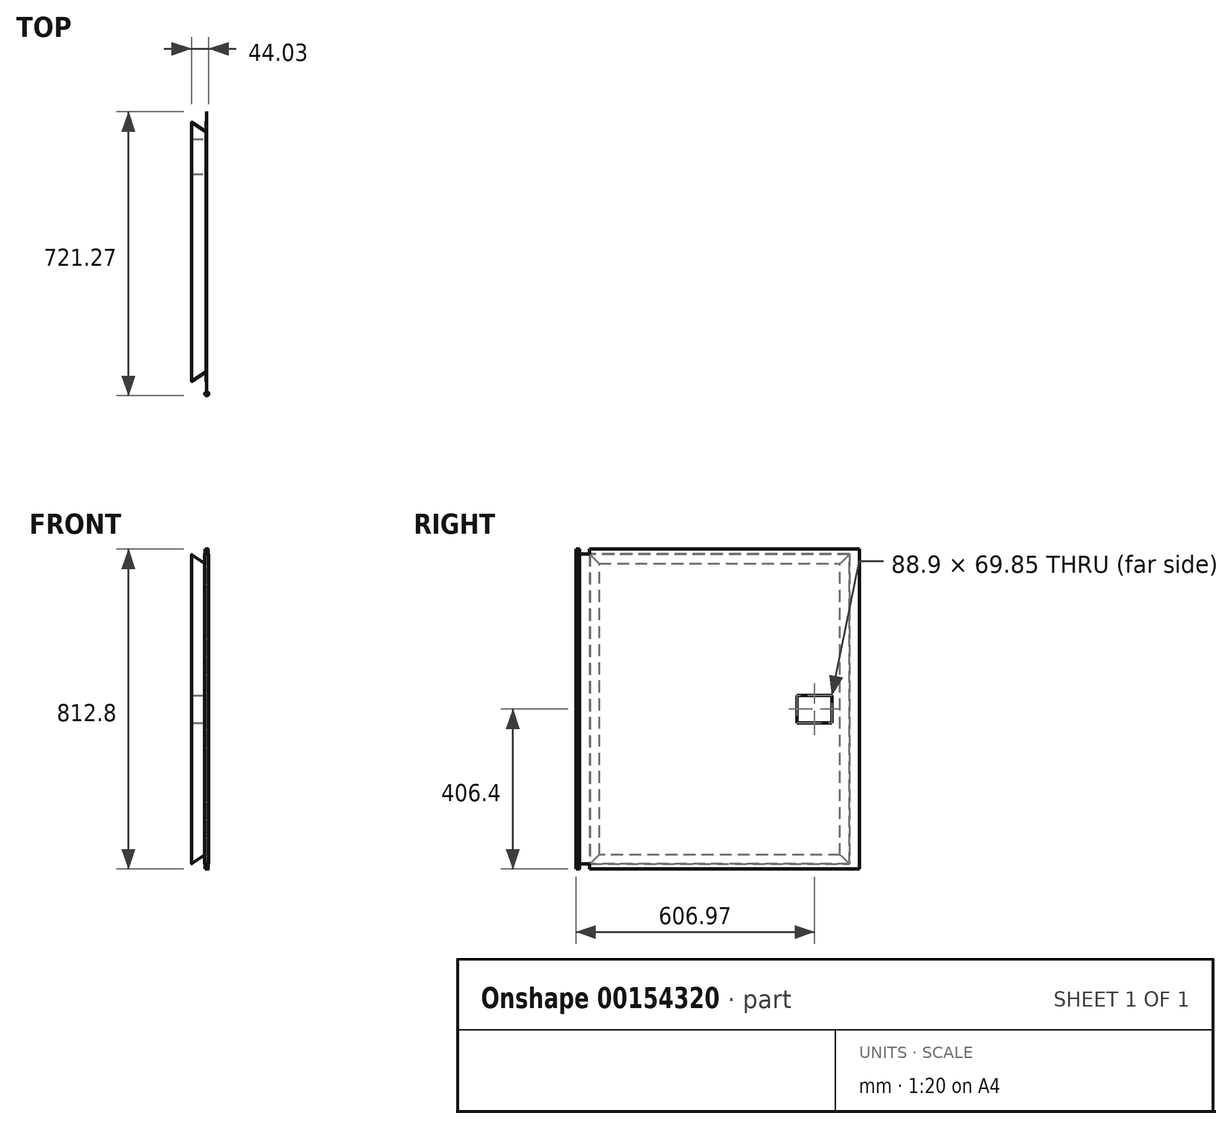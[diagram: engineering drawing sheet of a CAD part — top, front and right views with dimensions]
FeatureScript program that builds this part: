
annotation { "Feature Type Name" : "Feature", "Feature Type Description" : "" }
export const myFeature = defineFeature(function(context is Context, id is Id, definition is map)
    precondition{}
    {
        {
            var Q0;
            Q0=qCreatedBy(makeId("Right.planeOp"),FACE);
            var sketch = newSketch(context, id + "F0", { "sketchPlane" : qUnion([Q0])});
            skLineSegment(sketch, "E0.bottom", {"start": v(-330.2, 406.4) * mm, "end": v(355.6, 406.4) * mm});
            skLineSegment(sketch, "E0.left", {"start": v(-355.6, 393.7) * mm, "end": v(-355.6, -393.7) * mm});
            skLineSegment(sketch, "E0.right", {"start": v(355.6, 406.4) * mm, "end": v(355.6, -406.4) * mm});
            skPoint(sketch, "E0.middle", {"position": v(0, 0) * mm});
            skLineSegment(sketch, "E1", {"start": v(-355.6, 393.7) * mm, "end": v(-330.2, 393.7) * mm});
            skLineSegment(sketch, "E2", {"start": v(-330.2, 393.7) * mm, "end": v(-330.2, 406.4) * mm});
            skLineSegment(sketch, "E3", {"start": v(355.6, -406.4) * mm, "end": v(-330.2, -406.4) * mm});
            skLineSegment(sketch, "E4", {"start": v(-330.2, -406.4) * mm, "end": v(-330.2, -393.7) * mm});
            skLineSegment(sketch, "E5", {"start": v(-330.2, -393.7) * mm, "end": v(-355.6, -393.7) * mm});
            skLineSegment(sketch, "E6", {"start": v(-355.6, 0) * mm, "end": v(355.6, 0) * mm});
            skSolve(sketch);
        }
        {
            var Q0;
            Q0 = qSketchRegion(id + "F0", true);
            extrude(context, id + "F1", {"entities" : qUnion([Q0]), "oppositeDirection" : true, "depth" : 0.89 * mm});
        }
        {
            var Q0;
            Q0=makeQuery(id+"F1.opExtrude","CAP_FACE",FACE,{"disambiguationData":[OSD([sQuery(id+"F0.wireOp",EDGE,"E0.bottom"),sQuery(id+"F0.wireOp",EDGE,"E0.top"),sQuery(id+"F0.wireOp",EDGE,"E0.left"),sQuery(id+"F0.wireOp",EDGE,"E0.right")])],"isStart":false});
            var sketch = newSketch(context, id + "F2", { "sketchPlane" : qUnion([Q0])});
            skLineSegment(sketch, "E7.bottom", {"start": v(-330.2, 393.7) * mm, "end": v(330.2, 393.7) * mm});
            skLineSegment(sketch, "E7.top", {"start": v(-330.2, -393.7) * mm, "end": v(330.2, -393.7) * mm});
            skLineSegment(sketch, "E7.left", {"start": v(-330.2, 393.7) * mm, "end": v(-330.2, -393.7) * mm});
            skLineSegment(sketch, "E7.right", {"start": v(330.2, 393.7) * mm, "end": v(330.2, -393.7) * mm});
            skPoint(sketch, "E7.middle", {"position": v(0, 0) * mm});
            skSolve(sketch);
        }
        {
            var Q0;
            Q0 = qSketchRegion(id + "F2", true);
            extrude(context, id + "F3", {"entities" : qUnion([Q0]), "operationType" : NewBodyOperationType.ADD, "depth" : 38.1 * mm});
        }
        {
            var Q0;
            Q0=makeQuery(id+"F3.opExtrude","SWEPT_FACE",FACE,{"disambiguationData":[OSD([sQuery(id+"F2.wireOp",EDGE,"E7.left")])]});
            var sketch = newSketch(context, id + "F4", { "sketchPlane" : qUnion([Q0])});
            skLineSegment(sketch, "E8", {"start": v(38.99, 393.7) * mm, "end": v(38.99, -393.7) * mm});
            skLineSegment(sketch, "E9", {"start": v(38.99, 393.7) * mm, "end": v(2.13, 368.85) * mm});
            skLineSegment(sketch, "E10", {"start": v(2.13, 393.7) * mm, "end": v(2.13, -393.7) * mm});
            skLineSegment(sketch, "E11", {"start": v(38.99, -393.7) * mm, "end": v(2.13, -368.85) * mm});
            skSolve(sketch);
        }
        {
            var Q0;
            {var subQ3=sQuery(id+"F4.wireOp",EDGE,"E11");Q0=makeQuery(id+"F4.imprint","IMPRINT",FACE,{"disambiguationData":[TD([[makeQuery(id+"F4.imprint","IMPRINT",EDGE,{"derivedFrom":subQ3}),1.0]])]});}
            var Q1;
            {var subQ0=sQuery(id+"F4.wireOp",EDGE,"E9");Q1=makeQuery(id+"F4.imprint","IMPRINT",FACE,{"disambiguationData":[TD([[makeQuery(id+"F4.imprint","IMPRINT",EDGE,{"derivedFrom":subQ0}),-1.0]])]});}
            extrude(context, id + "F5", {"entities" : qUnion([Q0, Q1]), "operationType" : NewBodyOperationType.REMOVE, "endBound" : BoundingType.THROUGH_ALL, "oppositeDirection" : true, "depth" : 25.4 * mm});
        }
        {
            var Q0;
            {var subQ0=sQuery(id+"F4.wireOp",EDGE,"E10");var subQ2=sQuery(id+"F2.wireOp",EDGE,"E7.bottom");Q0=makeQuery(id+"F5.boolean.opBoolean","SPLIT",FACE,{"disambiguationData":[TD([makeQuery(id+"F5.opExtrude","SWEPT_FACE",FACE,{"disambiguationData":[OSD([subQ0]),TDD([makeQuery(id+"F4.imprint","IMPRINT",EDGE,{"disambiguationData":[TD([[makeQuery(id+"F4.imprint","INTERSECT",VERTEX,{"derivedFrom":[sQuery(id+"F4.wireOp",EDGE,"E9"),subQ0]}),1.0]])],"derivedFrom":subQ0})])]})])],"derivedFrom":makeQuery(id+"F3.opExtrude","SWEPT_FACE",FACE,{"disambiguationData":[OSD([subQ2])]})});}
            var sketch = newSketch(context, id + "F6", { "sketchPlane" : qUnion([Q0])});
            skLineSegment(sketch, "E12", {"start": v(-38.99, 330.2) * mm, "end": v(-2.13, 305.35) * mm});
            skLineSegment(sketch, "E13", {"start": v(-38.99, 330.2) * mm, "end": v(-2.13, 330.2) * mm});
            skLineSegment(sketch, "E14", {"start": v(-2.13, 305.35) * mm, "end": v(-2.13, 330.2) * mm});
            skLineSegment(sketch, "E15", {"start": v(-2.13, -305.35) * mm, "end": v(-2.13, -330.2) * mm});
            skLineSegment(sketch, "E16", {"start": v(-2.13, -330.2) * mm, "end": v(-38.99, -330.2) * mm});
            skLineSegment(sketch, "E17", {"start": v(-38.99, -330.2) * mm, "end": v(-2.13, -305.35) * mm});
            skSolve(sketch);
        }
        {
            var Q0;
            Q0=makeQuery(id+"F6.imprint","IMPRINT",FACE,{"disambiguationData":[TD([[makeQuery(id+"F6.imprint","IMPRINT",EDGE,{"derivedFrom":sQuery(id+"F6.wireOp",EDGE,"E15")}),1.0]])]});
            var Q1;
            Q1=makeQuery(id+"F6.imprint","IMPRINT",FACE,{"disambiguationData":[TD([[makeQuery(id+"F6.imprint","IMPRINT",EDGE,{"derivedFrom":sQuery(id+"F6.wireOp",EDGE,"E12")}),1.0]])]});
            extrude(context, id + "F7", {"entities" : qUnion([Q0, Q1]), "operationType" : NewBodyOperationType.REMOVE, "endBound" : BoundingType.THROUGH_ALL, "oppositeDirection" : true, "depth" : 25.4 * mm});
        }
        {
            var Q0;
            Q0=makeQuery(id+"F3.opExtrude","CAP_EDGE",EDGE,{"disambiguationData":[OSD([sQuery(id+"F2.wireOp",EDGE,"E7.top")])],"isStart":false});
            var Q1;
            Q1=makeQuery(id+"F3.opExtrude","CAP_EDGE",EDGE,{"disambiguationData":[OSD([sQuery(id+"F2.wireOp",EDGE,"E7.left")])],"isStart":false});
            var Q2;
            Q2=makeQuery(id+"F3.opExtrude","CAP_EDGE",EDGE,{"disambiguationData":[OSD([sQuery(id+"F2.wireOp",EDGE,"E7.bottom")])],"isStart":false});
            var Q3;
            Q3=makeQuery(id+"F3.opExtrude","CAP_EDGE",EDGE,{"disambiguationData":[OSD([sQuery(id+"F2.wireOp",EDGE,"E7.right")])],"isStart":false});
            fillet(context, id + "F8", {"entities" : qUnion([Q0, Q1, Q2, Q3]), "radius" : 1.27 * mm, "tangentPropagation" : true, "allowEdgeOverflow" : false});
        }
        {
            var Q0;
            Q0=makeQuery(id+"F7.boolean.opBoolean","COPY",EDGE,{"derivedFrom":makeQuery(id+"F7.opExtrude","SWEPT_EDGE",EDGE,{"disambiguationData":[OSD([sQuery(id+"F6.wireOp",EDGE,"9kJs9u86-Rynm-MJaU-KLCn-ISIbLXFeB2s4"),sQuery(id+"F6.wireOp",EDGE,"E12")])]})});
            var Q1;
            Q1=makeQuery(id+"F5.boolean.opBoolean","COPY",EDGE,{"derivedFrom":makeQuery(id+"F5.opExtrude","SWEPT_EDGE",EDGE,{"disambiguationData":[OSD([sQuery(id+"F4.wireOp",EDGE,"E9"),sQuery(id+"F4.wireOp",EDGE,"E10")])]})});
            var Q2;
            Q2=makeQuery(id+"F7.boolean.opBoolean","COPY",EDGE,{"derivedFrom":makeQuery(id+"F7.opExtrude","SWEPT_EDGE",EDGE,{"disambiguationData":[OSD([sQuery(id+"F6.wireOp",EDGE,"9kJs9u86-Rynm-MJaU-KLCn-ISIbLXFeB2s4"),sQuery(id+"F6.wireOp",EDGE,"ySAFRI99-aNW5-Edny-cf38-flcK1iuSa7Xp")])]})});
            var Q3;
            Q3=makeQuery(id+"F5.boolean.opBoolean","COPY",EDGE,{"derivedFrom":makeQuery(id+"F5.opExtrude","SWEPT_EDGE",EDGE,{"disambiguationData":[OSD([sQuery(id+"F4.wireOp",EDGE,"E10"),sQuery(id+"F4.wireOp",EDGE,"E11")])]})});
            fillet(context, id + "F9", {"entities" : qUnion([Q0, Q1, Q2, Q3]), "radius" : 1.27 * mm, "tangentPropagation" : true, "allowEdgeOverflow" : false});
        }
        {
            var Q0;
            Q0=makeQuery(id+"F1.opExtrude","CAP_FACE",FACE,{"disambiguationData":[OSD([sQuery(id+"F0.wireOp",EDGE,"E0.bottom"),sQuery(id+"F0.wireOp",EDGE,"E0.top"),sQuery(id+"F0.wireOp",EDGE,"E0.left"),sQuery(id+"F0.wireOp",EDGE,"E0.right")])],"isStart":true});
            var sketch = newSketch(context, id + "F10", { "sketchPlane" : qUnion([Q0])});
            skLineSegment(sketch, "E18", {"start": v(-355.6, 0) * mm, "end": v(355.6, 0) * mm});
            skLineSegment(sketch, "E19.bottom", {"start": v(196.85, 34.92) * mm, "end": v(285.75, 34.92) * mm});
            skLineSegment(sketch, "E19.top", {"start": v(196.85, -34.93) * mm, "end": v(285.75, -34.93) * mm});
            skLineSegment(sketch, "E19.left", {"start": v(196.85, 34.92) * mm, "end": v(196.85, -34.93) * mm});
            skLineSegment(sketch, "E19.right", {"start": v(285.75, 34.92) * mm, "end": v(285.75, -34.93) * mm});
            skPoint(sketch, "E19.middle", {"position": v(241.3, 0) * mm});
            skSolve(sketch);
        }
        {
            var Q0;
            Q0 = qSketchRegion(id + "F10", true);
            extrude(context, id + "F11", {"entities" : qUnion([Q0]), "operationType" : NewBodyOperationType.REMOVE, "endBound" : BoundingType.THROUGH_ALL, "oppositeDirection" : true, "depth" : 25.4 * mm});
        }
        {
            var Q0;
            Q0=qCreatedBy(makeId("Top.planeOp"),FACE);
            var sketch = newSketch(context, id + "F12", { "sketchPlane" : qUnion([Q0])});
            skCircle(sketch, "E20", {"center": v(0, -360.64) * mm, "radius": 5.04 * mm});
            skCircle(sketch, "E21", {"center": v(0, -360.64) * mm, "radius": 3.97 * mm});
            skSolve(sketch);
        }
        {
            var Q0;
            Q0 = qSketchRegion(id + "F12", true);
            var Q1;
            Q1=makeQuery(id+"F3.boolean.opBoolean","MERGE",FACE,{"derivedFrom":[makeQuery(id+"F1.opExtrude","SWEPT_FACE",FACE,{"disambiguationData":[OSD([sQuery(id+"F0.wireOp",EDGE,"E1")])]}),makeQuery(id+"F3.opExtrude","SWEPT_FACE",FACE,{"disambiguationData":[OSD([sQuery(id+"F2.wireOp",EDGE,"E7.bottom")])]})]});
            var Q2;
            Q2=makeQuery(id+"F3.boolean.opBoolean","MERGE",FACE,{"derivedFrom":[makeQuery(id+"F1.opExtrude","SWEPT_FACE",FACE,{"disambiguationData":[OSD([sQuery(id+"F0.wireOp",EDGE,"E5")])]}),makeQuery(id+"F3.opExtrude","SWEPT_FACE",FACE,{"disambiguationData":[OSD([sQuery(id+"F2.wireOp",EDGE,"E7.top")])]})]});
            extrude(context, id + "F13", {"entities" : qUnion([Q0]), "endBound" : BoundingType.UP_TO_SURFACE, "endBoundEntityFace" : qUnion([Q1]), "depth" : 25.4 * mm, "hasSecondDirection" : true, "secondDirectionBound" : SecondDirectionBoundingType.UP_TO_SURFACE, "secondDirectionOppositeDirection" : true, "secondDirectionBoundEntityFace" : qUnion([Q2]), "secondDirectionDepth" : 25.4 * mm});
        }
        {
            var Q0;
            Q0=qCreatedBy(makeId("Top.planeOp"),FACE);
            var sketch = newSketch(context, id + "F14", { "sketchPlane" : qUnion([Q0])});
            skCircle(sketch, "E22", {"center": v(0, -360.64) * mm, "radius": 3.97 * mm});
            skSolve(sketch);
        }
        {
            var Q0;
            Q0 = qSketchRegion(id + "F14", true);
            var Q1;
            Q1=makeQuery(id+"F1.opExtrude","SWEPT_FACE",FACE,{"disambiguationData":[OSD([sQuery(id+"F0.wireOp",EDGE,"E0.bottom")])]});
            var Q2;
            Q2=makeQuery(id+"F1.opExtrude","SWEPT_FACE",FACE,{"disambiguationData":[OSD([sQuery(id+"F0.wireOp",EDGE,"E3")])]});
            extrude(context, id + "F15", {"entities" : qUnion([Q0]), "operationType" : NewBodyOperationType.ADD, "endBound" : BoundingType.UP_TO_SURFACE, "endBoundEntityFace" : qUnion([Q1]), "depth" : 25.4 * mm, "hasSecondDirection" : true, "secondDirectionBound" : SecondDirectionBoundingType.UP_TO_SURFACE, "secondDirectionOppositeDirection" : true, "secondDirectionBoundEntityFace" : qUnion([Q2]), "secondDirectionDepth" : 25.4 * mm});
        }
    });
